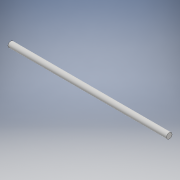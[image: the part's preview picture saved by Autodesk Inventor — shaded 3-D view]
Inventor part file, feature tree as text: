
AUTODESK INVENTOR PART (.ipt)
format: ipt  version: 2018 (Build 220112000, 112)  size: 90,112 bytes
history: native  units: mm
features: other x1, extrude x1, sketch x1
ambient origin geometry x8: Origin, YZ Plane, XZ Plane, XY Plane, X Axis, Y Axis, Z Axis, Center Point
bodies: Body1 (feature_tree)
feature tree (3):
  other  "ソリッド1"
  extrude  "押し出し1"  Depth=14.0mm
  sketch  "スケッチ1"
